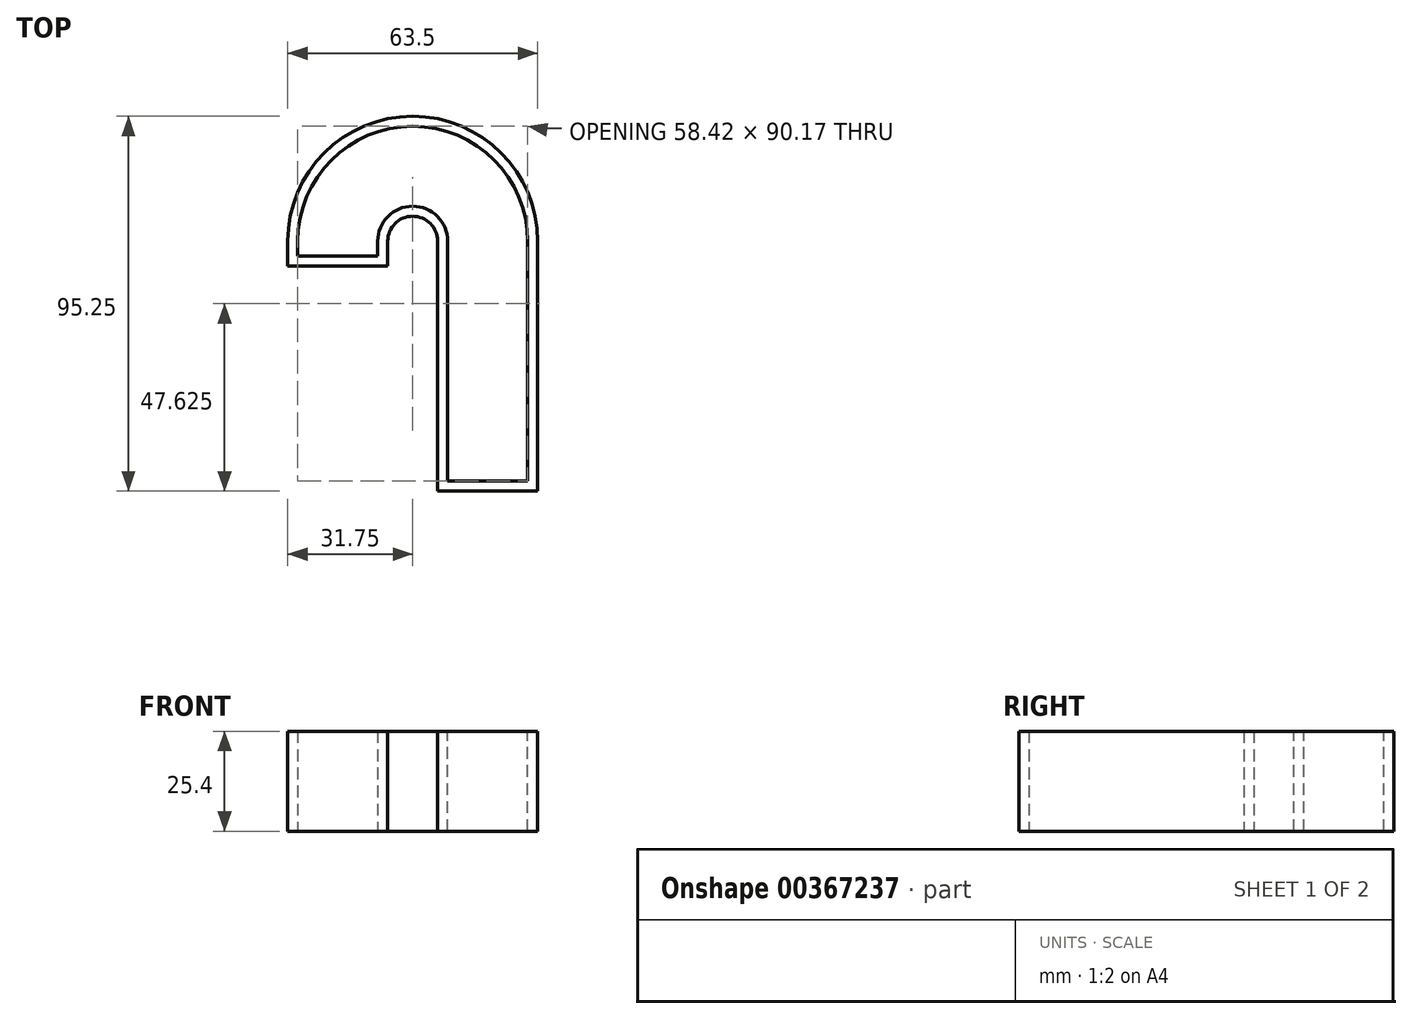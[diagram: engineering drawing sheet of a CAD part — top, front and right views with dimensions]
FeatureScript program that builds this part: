
annotation { "Feature Type Name" : "Feature", "Feature Type Description" : "" }
export const myFeature = defineFeature(function(context is Context, id is Id, definition is map)
    precondition{}
    {
        {
            var Q0;
            Q0=qCreatedBy(makeId("Top.planeOp"),FACE);
            var sketch = newSketch(context, id + "F0", { "sketchPlane" : qUnion([Q0])});
            skLineSegment(sketch, "E0", {"start": v(0, 0) * mm, "end": v(0, 63.5) * mm});
            skArc(sketch, "E1", {"start": v(0, 63.5) * mm, "mid": v(-19.05, 82.55) * mm, "end": v(-38.1, 63.5) * mm});
            skLineSegment(sketch, "E2", {"start": v(-38.1, 63.5) * mm, "end": v(-38.1, 57.15) * mm});
            skSolve(sketch);
        }
        {
            var Q0;
            Q0=qCreatedBy(makeId("Front.planeOp"),FACE);
            var sketch = newSketch(context, id + "F1", { "sketchPlane" : qUnion([Q0])});
            skLineSegment(sketch, "E3.bottom", {"start": v(-12.7, 12.7) * mm, "end": v(12.7, 12.7) * mm});
            skLineSegment(sketch, "E3.top", {"start": v(-12.7, -12.7) * mm, "end": v(12.7, -12.7) * mm});
            skLineSegment(sketch, "E3.left", {"start": v(-12.7, 12.7) * mm, "end": v(-12.7, -12.7) * mm});
            skLineSegment(sketch, "E3.right", {"start": v(12.7, 12.7) * mm, "end": v(12.7, -12.7) * mm});
            skPoint(sketch, "E4", {"position": v(0, 12.7) * mm});
            skPoint(sketch, "E5", {"position": v(12.7, 0) * mm});
            skSolve(sketch);
        }
        {
            var Q0;
            Q0=makeQuery(id+"F1.imprint","IMPRINT",FACE,{"disambiguationData":[TD([[makeQuery(id+"F1.imprint","IMPRINT",EDGE,{"derivedFrom":sQuery(id+"F1.wireOp",EDGE,"E3.bottom")}),-1.0]])]});
            var Q1;
            Q1=sQuery(id+"F0.wireOp",EDGE,"E0");
            var Q2;
            Q2=sQuery(id+"F0.wireOp",EDGE,"E1");
            var Q3;
            Q3=sQuery(id+"F0.wireOp",EDGE,"E2");
            sweep(context, id + "F2", {"profiles" : qUnion([Q0]), "path" : qUnion([Q1, Q2, Q3])});
        }
        {
            var Q0;
            Q0=makeQuery(id+"F2.opSweep","SWEPT_FACE",FACE,{"disambiguationData":[OSD([sQuery(id+"F0.wireOp",EDGE,"E0"),sQuery(id+"F1.wireOp",EDGE,"E3.bottom")])]});
            shell(context, id + "F3", {"entities" : qUnion([Q0]), "thickness" : 2.54 * mm});
        }
        {
            var Q0;
            Q0=makeQuery(id+"F3.opShell","OFFSET_FACE",FACE,{"disambiguationData":[OSD([sQuery(id+"F0.wireOp",EDGE,"E0"),sQuery(id+"F1.wireOp",EDGE,"E3.top")])]});
            extrude(context, id + "F4", {"entities" : qUnion([Q0]), "operationType" : NewBodyOperationType.REMOVE, "endBound" : BoundingType.THROUGH_ALL, "oppositeDirection" : true, "depth" : 25.4 * mm});
        }
    });
